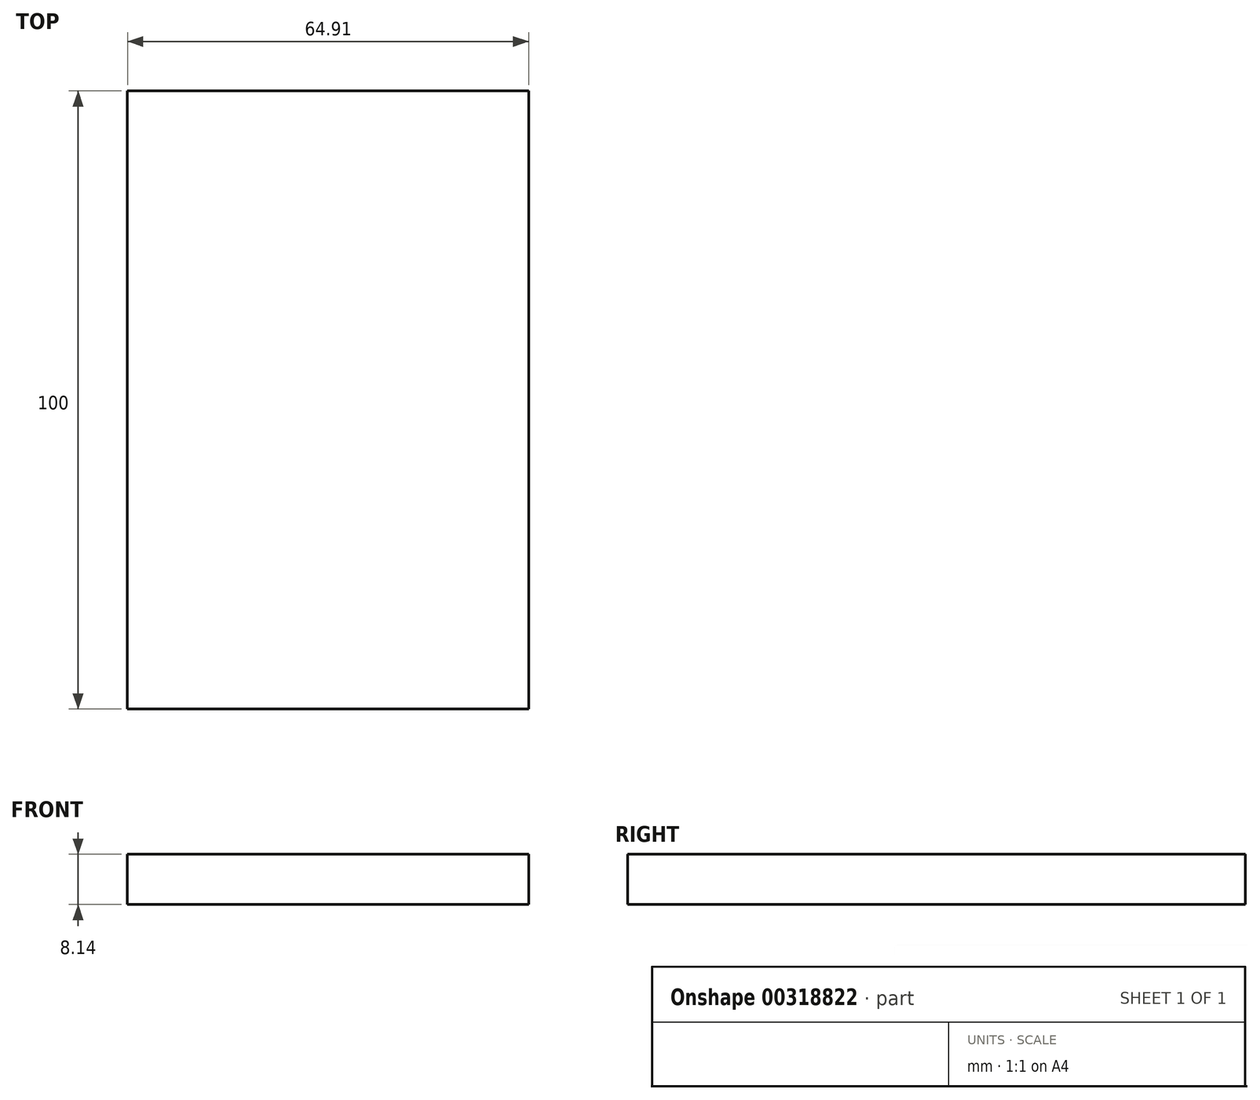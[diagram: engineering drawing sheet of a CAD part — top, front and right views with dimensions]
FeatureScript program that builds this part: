
annotation { "Feature Type Name" : "Feature", "Feature Type Description" : "" }
export const myFeature = defineFeature(function(context is Context, id is Id, definition is map)
    precondition{}
    {
        {
            var Q0;
            Q0=qCreatedBy(makeId("Front.planeOp"),FACE);
            var sketch = newSketch(context, id + "F0", { "sketchPlane" : qUnion([Q0])});
            skLineSegment(sketch, "E0.bottom", {"start": v(-33.8, 0) * mm, "end": v(31.12, 0) * mm});
            skLineSegment(sketch, "E0.top", {"start": v(-33.8, 8.14) * mm, "end": v(31.12, 8.14) * mm});
            skLineSegment(sketch, "E0.left", {"start": v(-33.8, 0) * mm, "end": v(-33.8, 8.14) * mm});
            skLineSegment(sketch, "E0.right", {"start": v(31.12, 0) * mm, "end": v(31.12, 8.14) * mm});
            skSolve(sketch);
        }
        {
            var Q0;
            Q0=makeQuery(id+"F0.imprint","IMPRINT",FACE,{"disambiguationData":[TD([[makeQuery(id+"F0.imprint","IMPRINT",EDGE,{"derivedFrom":sQuery(id+"F0.wireOp",EDGE,"E0.bottom")}),1.0]])]});
            extrude(context, id + "F1", {"entities" : qUnion([Q0]), "depth" : 100 * mm});
        }
    });
